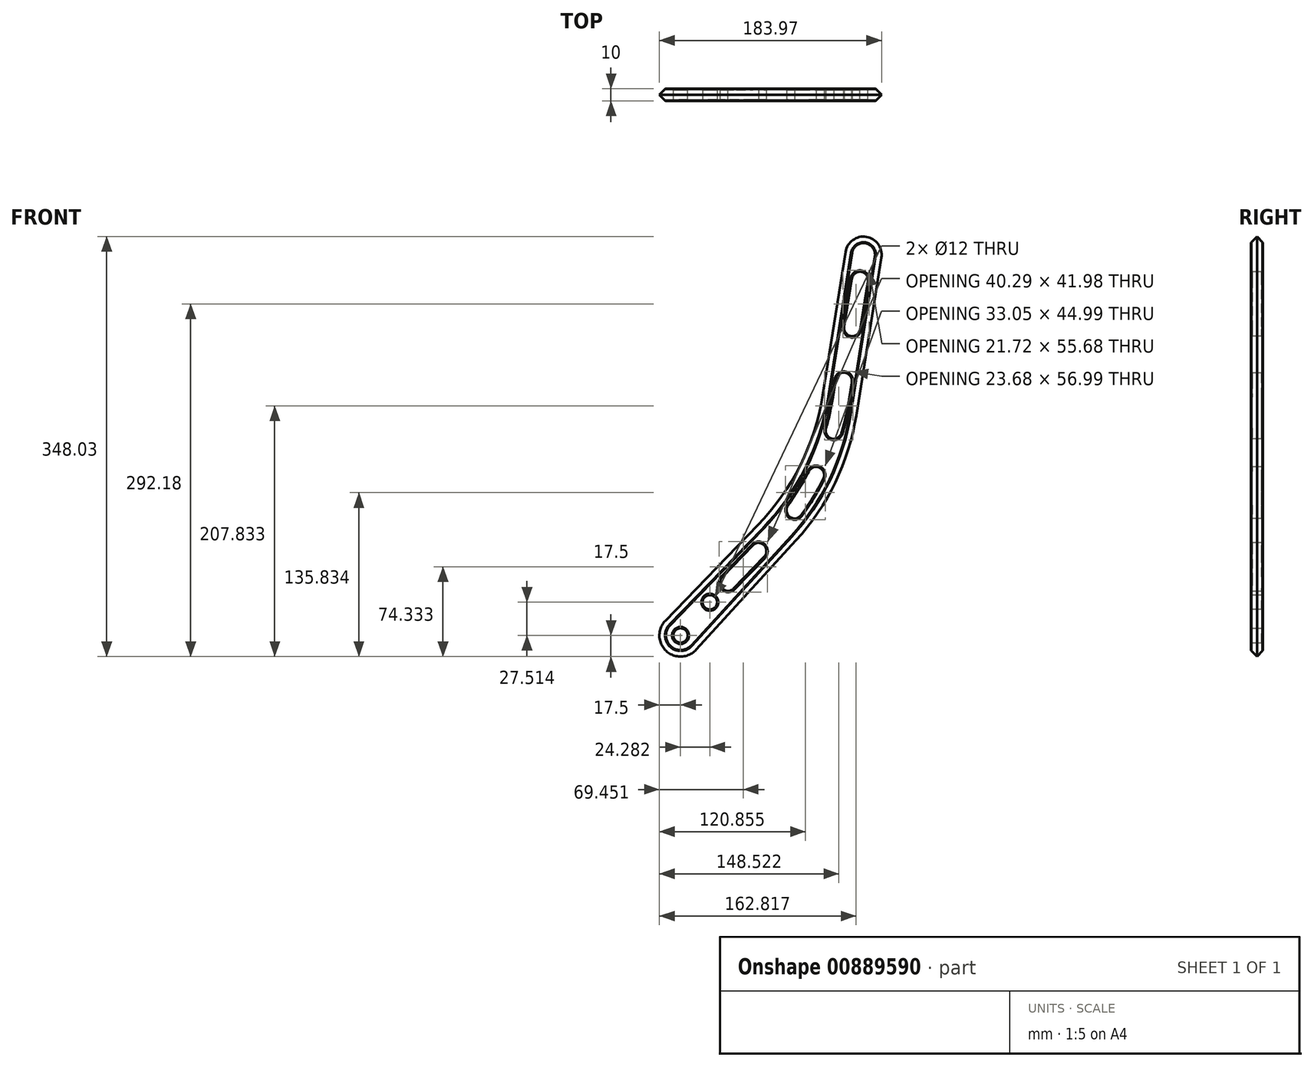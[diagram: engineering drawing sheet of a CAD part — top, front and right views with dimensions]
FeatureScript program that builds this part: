
annotation { "Feature Type Name" : "Feature", "Feature Type Description" : "" }
export const myFeature = defineFeature(function(context is Context, id is Id, definition is map)
    precondition{}
    {
        {
            var Q0;
            Q0=qCreatedBy(makeId("Front.planeOp"),FACE);
            var sketch = newSketch(context, id + "F0", { "sketchPlane" : qUnion([Q0])});
            skCircle(sketch, "E0", {"center": v(0, 0) * mm, "radius": 6 * mm});
            skArc(sketch, "E1", {"start": v(-12.58, 12.17) * mm, "mid": v(-11.98, -12.75) * mm, "end": v(12.92, -11.8) * mm});
            skArc(sketch, "E2", {"start": v(166.29, 313.17) * mm, "mid": v(153.83, 330.34) * mm, "end": v(136.66, 317.88) * mm});
            skLineSegment(sketch, "E3", {"start": v(-12.58, 12.17) * mm, "end": v(107.83, 136.69) * mm});
            skLineSegment(sketch, "E4", {"start": v(107.83, 136.69) * mm, "end": v(136.66, 317.88) * mm});
            skLineSegment(sketch, "E5", {"start": v(12.92, -11.8) * mm, "end": v(136.03, 122.98) * mm});
            skLineSegment(sketch, "E6", {"start": v(136.03, 122.98) * mm, "end": v(166.29, 313.17) * mm});
            skSolve(sketch);
        }
        {
            var Q0;
            Q0=makeQuery(id+"F0.imprint","IMPRINT",FACE,{"disambiguationData":[TD([[makeQuery(id+"F0.imprint","IMPRINT",EDGE,{"derivedFrom":sQuery(id+"F0.wireOp",EDGE,"E0")}),-1.0]])]});
            extrude(context, id + "F1", {"entities" : qUnion([Q0]), "depth" : 10 * mm, "offsetDistance" : 25 * mm});
        }
        {
            var Q0;
            Q0=makeQuery(id+"F1.opExtrude","SWEPT_EDGE",EDGE,{"disambiguationData":[OSD([sQuery(id+"F0.wireOp",EDGE,"E3"),sQuery(id+"F0.wireOp",EDGE,"E4")])]});
            var Q1;
            Q1=makeQuery(id+"F1.opExtrude","SWEPT_EDGE",EDGE,{"disambiguationData":[OSD([sQuery(id+"F0.wireOp",EDGE,"E5"),sQuery(id+"F0.wireOp",EDGE,"E6")])]});
            fillet(context, id + "F2", {"entities" : qUnion([Q0, Q1]), "radius" : 200 * mm, "tangentPropagation" : true, "allowEdgeOverflow" : false});
        }
        {
            var Q0;
            {var subQ0=sQuery(id+"F0.wireOp",EDGE,"E4");var subQ1=sQuery(id+"F0.wireOp",EDGE,"E3");Q0=makeQuery(id+"F2.opFillet","BLEND_EDGE",EDGE,{"blendedFrom":[makeQuery(id+"F1.opExtrude","SWEPT_EDGE",EDGE,{"disambiguationData":[OSD([subQ1,subQ0])]}),makeQuery(id+"F1.opExtrude","CAP_FACE",FACE,{"disambiguationData":[OSD([sQuery(id+"F0.wireOp",EDGE,"E0"),sQuery(id+"F0.wireOp",EDGE,"E1"),sQuery(id+"F0.wireOp",EDGE,"E2"),subQ1,subQ0,sQuery(id+"F0.wireOp",EDGE,"E5"),sQuery(id+"F0.wireOp",EDGE,"E6")])],"isStart":false})],"blendedInto":[makeQuery(id+"F1.opExtrude","CAP_FACE",FACE,{"disambiguationData":[OSD([sQuery(id+"F0.wireOp",EDGE,"E0"),sQuery(id+"F0.wireOp",EDGE,"E1"),sQuery(id+"F0.wireOp",EDGE,"E2"),subQ1,subQ0,sQuery(id+"F0.wireOp",EDGE,"E5"),sQuery(id+"F0.wireOp",EDGE,"E6")])],"isStart":false})]});}
            var Q1;
            {var subQ0=sQuery(id+"F0.wireOp",EDGE,"E4");var subQ1=sQuery(id+"F0.wireOp",EDGE,"E3");Q1=makeQuery(id+"F2.opFillet","BLEND_EDGE",EDGE,{"blendedFrom":[makeQuery(id+"F1.opExtrude","SWEPT_EDGE",EDGE,{"disambiguationData":[OSD([subQ1,subQ0])]}),makeQuery(id+"F1.opExtrude","CAP_FACE",FACE,{"disambiguationData":[OSD([sQuery(id+"F0.wireOp",EDGE,"E0"),sQuery(id+"F0.wireOp",EDGE,"E1"),sQuery(id+"F0.wireOp",EDGE,"E2"),subQ1,subQ0,sQuery(id+"F0.wireOp",EDGE,"E5"),sQuery(id+"F0.wireOp",EDGE,"E6")])],"isStart":true})],"blendedInto":[makeQuery(id+"F1.opExtrude","CAP_FACE",FACE,{"disambiguationData":[OSD([sQuery(id+"F0.wireOp",EDGE,"E0"),sQuery(id+"F0.wireOp",EDGE,"E1"),sQuery(id+"F0.wireOp",EDGE,"E2"),subQ1,subQ0,sQuery(id+"F0.wireOp",EDGE,"E5"),sQuery(id+"F0.wireOp",EDGE,"E6")])],"isStart":true})]});}
            chamfer(context, id + "F3", {"entities" : qUnion([Q0, Q1]), "width" : 5 * mm, "tangentPropagation" : true});
        }
        {
            var Q0;
            Q0=makeQuery(id+"F1.opExtrude","CAP_FACE",FACE,{"disambiguationData":[OSD([sQuery(id+"F0.wireOp",EDGE,"E0"),sQuery(id+"F0.wireOp",EDGE,"E1"),sQuery(id+"F0.wireOp",EDGE,"E2"),sQuery(id+"F0.wireOp",EDGE,"E3"),sQuery(id+"F0.wireOp",EDGE,"E4"),sQuery(id+"F0.wireOp",EDGE,"E5"),sQuery(id+"F0.wireOp",EDGE,"E6")])],"isStart":false});
            var sketch = newSketch(context, id + "F4", { "sketchPlane" : qUnion([Q0])});
            skCircle(sketch, "E7", {"center": v(24.28, 27.51) * mm, "radius": 6 * mm});
            skSolve(sketch);
        }
        {
            var Q0;
            Q0=makeQuery(id+"F4.imprint","IMPRINT",FACE,{"disambiguationData":[TD([[makeQuery(id+"F4.imprint","IMPRINT",EDGE,{"derivedFrom":sQuery(id+"F4.wireOp",EDGE,"E7")}),1.0]])]});
            extrude(context, id + "F5", {"entities" : qUnion([Q0]), "operationType" : NewBodyOperationType.REMOVE, "oppositeDirection" : true, "depth" : 25 * mm, "offsetDistance" : 25 * mm});
        }
        {
            var Q0;
            Q0=makeQuery(id+"F1.opExtrude","CAP_FACE",FACE,{"disambiguationData":[OSD([sQuery(id+"F0.wireOp",EDGE,"E0"),sQuery(id+"F0.wireOp",EDGE,"E1"),sQuery(id+"F0.wireOp",EDGE,"E2"),sQuery(id+"F0.wireOp",EDGE,"E3"),sQuery(id+"F0.wireOp",EDGE,"E4"),sQuery(id+"F0.wireOp",EDGE,"E5"),sQuery(id+"F0.wireOp",EDGE,"E6")])],"isStart":false});
            var sketch = newSketch(context, id + "F6", { "sketchPlane" : qUnion([Q0])});
            skArc(sketch, "E8", {"start": v(80.5, 96.83) * mm, "mid": v(95.65, 117.48) * mm, "end": v(108.17, 139.83) * mm});
            skArc(sketch, "E9", {"start": v(79.85, 76.02) * mm, "mid": v(80.24, 76.43) * mm, "end": v(80.63, 76.83) * mm});
            skLineSegment(sketch, "E10", {"start": v(126.25, 197.61) * mm, "end": v(129.47, 217.83) * mm});
            skLineSegment(sketch, "E11", {"start": v(156.39, 301.53) * mm, "end": v(147.85, 247.83) * mm});
            skLineSegment(sketch, "E12", {"start": v(61.95, 76.83) * mm, "end": v(23.27, 36.83) * mm});
            skLineSegment(sketch, "E13", {"start": v(41.96, 36.83) * mm, "end": v(79.85, 76.02) * mm});
            skPoint(sketch, "E13.startSnap0", {"position": v(50.57, 36.83) * mm});
            skLineSegment(sketch, "E14", {"start": v(142.79, 301.53) * mm, "end": v(156.39, 301.53) * mm});
            skLineSegment(sketch, "E15", {"start": v(23.27, 36.83) * mm, "end": v(41.96, 36.83) * mm});
            skLineSegment(sketch, "E16", {"start": v(61.95, 76.83) * mm, "end": v(80.63, 76.83) * mm});
            skLineSegment(sketch, "E17", {"start": v(80.5, 96.83) * mm, "end": v(97.63, 96.83) * mm});
            skLineSegment(sketch, "E18", {"start": v(108.17, 139.83) * mm, "end": v(122.98, 139.83) * mm});
            skLineSegment(sketch, "E19", {"start": v(117.6, 162.83) * mm, "end": v(131.76, 162.83) * mm});
            skLineSegment(sketch, "E20", {"start": v(134.24, 247.83) * mm, "end": v(147.85, 247.83) * mm});
            skLineSegment(sketch, "E21", {"start": v(129.47, 217.83) * mm, "end": v(143.08, 217.83) * mm});
            skLineSegment(sketch, "E22.trimOffspring", {"start": v(134.24, 247.83) * mm, "end": v(142.79, 301.53) * mm});
            skLineSegment(sketch, "E23.trimOffspring", {"start": v(143.08, 217.83) * mm, "end": v(139.52, 195.5) * mm});
            skArc(sketch, "E24.trimOffspring", {"start": v(117.6, 162.83) * mm, "mid": v(122.68, 180.04) * mm, "end": v(126.25, 197.61) * mm});
            skArc(sketch, "E25.trimOffspring", {"start": v(131.76, 162.83) * mm, "mid": v(136.26, 179.02) * mm, "end": v(139.52, 195.5) * mm});
            skArc(sketch, "E26.trimOffspring", {"start": v(97.63, 96.83) * mm, "mid": v(111.52, 117.62) * mm, "end": v(122.98, 139.83) * mm});
            skSolve(sketch);
        }
        {
            var Q0;
            Q0=makeQuery(id+"F6.imprint","IMPRINT",FACE,{"disambiguationData":[TD([[makeQuery(id+"F6.imprint","IMPRINT",EDGE,{"derivedFrom":sQuery(id+"F6.wireOp",EDGE,"E9")}),1.0]])]});
            var Q1;
            Q1=makeQuery(id+"F6.imprint","IMPRINT",FACE,{"disambiguationData":[TD([[makeQuery(id+"F6.imprint","IMPRINT",EDGE,{"derivedFrom":sQuery(id+"F6.wireOp",EDGE,"E8")}),-1.0]])]});
            var Q2;
            Q2=makeQuery(id+"F6.imprint","IMPRINT",FACE,{"disambiguationData":[TD([[makeQuery(id+"F6.imprint","IMPRINT",EDGE,{"derivedFrom":sQuery(id+"F6.wireOp",EDGE,"E10")}),-1.0]])]});
            var Q3;
            Q3=makeQuery(id+"F6.imprint","IMPRINT",FACE,{"disambiguationData":[TD([[makeQuery(id+"F6.imprint","IMPRINT",EDGE,{"derivedFrom":sQuery(id+"F6.wireOp",EDGE,"E11")}),-1.0]])]});
            extrude(context, id + "F7", {"entities" : qUnion([Q0, Q1, Q2, Q3]), "operationType" : NewBodyOperationType.REMOVE, "oppositeDirection" : true, "depth" : 25 * mm, "offsetDistance" : 25 * mm});
        }
        {
            var Q0;
            Q0=makeQuery(id+"F7.boolean.opBoolean","COPY",EDGE,{"derivedFrom":makeQuery(id+"F7.opExtrude","SWEPT_EDGE",EDGE,{"disambiguationData":[OSD([sQuery(id+"F6.wireOp",EDGE,"E12"),sQuery(id+"F6.wireOp",EDGE,"E15")])]})});
            var Q1;
            Q1=makeQuery(id+"F7.boolean.opBoolean","COPY",EDGE,{"derivedFrom":makeQuery(id+"F7.opExtrude","SWEPT_EDGE",EDGE,{"disambiguationData":[OSD([sQuery(id+"F6.wireOp",EDGE,"E13"),sQuery(id+"F6.wireOp",EDGE,"E15")])]})});
            var Q2;
            Q2=makeQuery(id+"F7.boolean.opBoolean","COPY",EDGE,{"derivedFrom":makeQuery(id+"F7.opExtrude","SWEPT_EDGE",EDGE,{"disambiguationData":[OSD([sQuery(id+"F6.wireOp",EDGE,"E12"),sQuery(id+"F6.wireOp",EDGE,"E16")])]})});
            var Q3;
            Q3=makeQuery(id+"F7.boolean.opBoolean","COPY",EDGE,{"derivedFrom":makeQuery(id+"F7.opExtrude","SWEPT_EDGE",EDGE,{"disambiguationData":[OSD([sQuery(id+"F6.wireOp",EDGE,"E9"),sQuery(id+"F6.wireOp",EDGE,"E16")])]})});
            var Q4;
            Q4=makeQuery(id+"F7.boolean.opBoolean","COPY",EDGE,{"derivedFrom":makeQuery(id+"F7.opExtrude","SWEPT_EDGE",EDGE,{"disambiguationData":[OSD([sQuery(id+"F6.wireOp",EDGE,"E8"),sQuery(id+"F6.wireOp",EDGE,"E17")])]})});
            var Q5;
            Q5=makeQuery(id+"F7.boolean.opBoolean","COPY",EDGE,{"derivedFrom":makeQuery(id+"F7.opExtrude","SWEPT_EDGE",EDGE,{"disambiguationData":[OSD([sQuery(id+"F6.wireOp",EDGE,"E17"),sQuery(id+"F6.wireOp",EDGE,"E26.trimOffspring")])]})});
            var Q6;
            Q6=makeQuery(id+"F7.boolean.opBoolean","COPY",EDGE,{"derivedFrom":makeQuery(id+"F7.opExtrude","SWEPT_EDGE",EDGE,{"disambiguationData":[OSD([sQuery(id+"F6.wireOp",EDGE,"E8"),sQuery(id+"F6.wireOp",EDGE,"E18")])]})});
            var Q7;
            Q7=makeQuery(id+"F7.boolean.opBoolean","COPY",EDGE,{"derivedFrom":makeQuery(id+"F7.opExtrude","SWEPT_EDGE",EDGE,{"disambiguationData":[OSD([sQuery(id+"F6.wireOp",EDGE,"E18"),sQuery(id+"F6.wireOp",EDGE,"E26.trimOffspring")])]})});
            var Q8;
            Q8=makeQuery(id+"F7.boolean.opBoolean","COPY",EDGE,{"derivedFrom":makeQuery(id+"F7.opExtrude","SWEPT_EDGE",EDGE,{"disambiguationData":[OSD([sQuery(id+"F6.wireOp",EDGE,"E19"),sQuery(id+"F6.wireOp",EDGE,"E24.trimOffspring")])]})});
            var Q9;
            Q9=makeQuery(id+"F7.boolean.opBoolean","COPY",EDGE,{"derivedFrom":makeQuery(id+"F7.opExtrude","SWEPT_EDGE",EDGE,{"disambiguationData":[OSD([sQuery(id+"F6.wireOp",EDGE,"E19"),sQuery(id+"F6.wireOp",EDGE,"E25.trimOffspring")])]})});
            var Q10;
            Q10=makeQuery(id+"F7.boolean.opBoolean","COPY",EDGE,{"derivedFrom":makeQuery(id+"F7.opExtrude","SWEPT_EDGE",EDGE,{"disambiguationData":[OSD([sQuery(id+"F6.wireOp",EDGE,"E21"),sQuery(id+"F6.wireOp",EDGE,"E23.trimOffspring")])]})});
            var Q11;
            Q11=makeQuery(id+"F7.boolean.opBoolean","COPY",EDGE,{"derivedFrom":makeQuery(id+"F7.opExtrude","SWEPT_EDGE",EDGE,{"disambiguationData":[OSD([sQuery(id+"F6.wireOp",EDGE,"E10"),sQuery(id+"F6.wireOp",EDGE,"E21")])]})});
            var Q12;
            Q12=makeQuery(id+"F7.boolean.opBoolean","COPY",EDGE,{"derivedFrom":makeQuery(id+"F7.opExtrude","SWEPT_EDGE",EDGE,{"disambiguationData":[OSD([sQuery(id+"F6.wireOp",EDGE,"E14"),sQuery(id+"F6.wireOp",EDGE,"E22.trimOffspring")])]})});
            var Q13;
            Q13=makeQuery(id+"F7.boolean.opBoolean","COPY",EDGE,{"derivedFrom":makeQuery(id+"F7.opExtrude","SWEPT_EDGE",EDGE,{"disambiguationData":[OSD([sQuery(id+"F6.wireOp",EDGE,"E11"),sQuery(id+"F6.wireOp",EDGE,"E14")])]})});
            var Q14;
            Q14=makeQuery(id+"F7.boolean.opBoolean","COPY",EDGE,{"derivedFrom":makeQuery(id+"F7.opExtrude","SWEPT_EDGE",EDGE,{"disambiguationData":[OSD([sQuery(id+"F6.wireOp",EDGE,"E20"),sQuery(id+"F6.wireOp",EDGE,"E22.trimOffspring")])]})});
            var Q15;
            Q15=makeQuery(id+"F7.boolean.opBoolean","COPY",EDGE,{"derivedFrom":makeQuery(id+"F7.opExtrude","SWEPT_EDGE",EDGE,{"disambiguationData":[OSD([sQuery(id+"F6.wireOp",EDGE,"E11"),sQuery(id+"F6.wireOp",EDGE,"E20")])]})});
            fillet(context, id + "F8", {"entities" : qUnion([Q0, Q1, Q2, Q3, Q4, Q5, Q6, Q7, Q8, Q9, Q10, Q11, Q12, Q13, Q14, Q15]), "radius" : 7 * mm, "tangentPropagation" : true, "allowEdgeOverflow" : false});
        }
        {
            var Q0;
            Q0=makeQuery(id+"F1.opExtrude","CAP_FACE",FACE,{"disambiguationData":[OSD([sQuery(id+"F0.wireOp",EDGE,"E0"),sQuery(id+"F0.wireOp",EDGE,"E1"),sQuery(id+"F0.wireOp",EDGE,"E2"),sQuery(id+"F0.wireOp",EDGE,"E3"),sQuery(id+"F0.wireOp",EDGE,"E4"),sQuery(id+"F0.wireOp",EDGE,"E5"),sQuery(id+"F0.wireOp",EDGE,"E6")])],"isStart":false});
            var Q1;
            Q1=makeQuery(id+"F1.opExtrude","CAP_FACE",FACE,{"disambiguationData":[OSD([sQuery(id+"F0.wireOp",EDGE,"E0"),sQuery(id+"F0.wireOp",EDGE,"E1"),sQuery(id+"F0.wireOp",EDGE,"E2"),sQuery(id+"F0.wireOp",EDGE,"E3"),sQuery(id+"F0.wireOp",EDGE,"E4"),sQuery(id+"F0.wireOp",EDGE,"E5"),sQuery(id+"F0.wireOp",EDGE,"E6")])],"isStart":true});
            chamfer(context, id + "F9", {"entities" : qUnion([Q0, Q1]), "width" : 1 * mm, "tangentPropagation" : true});
        }
    });
